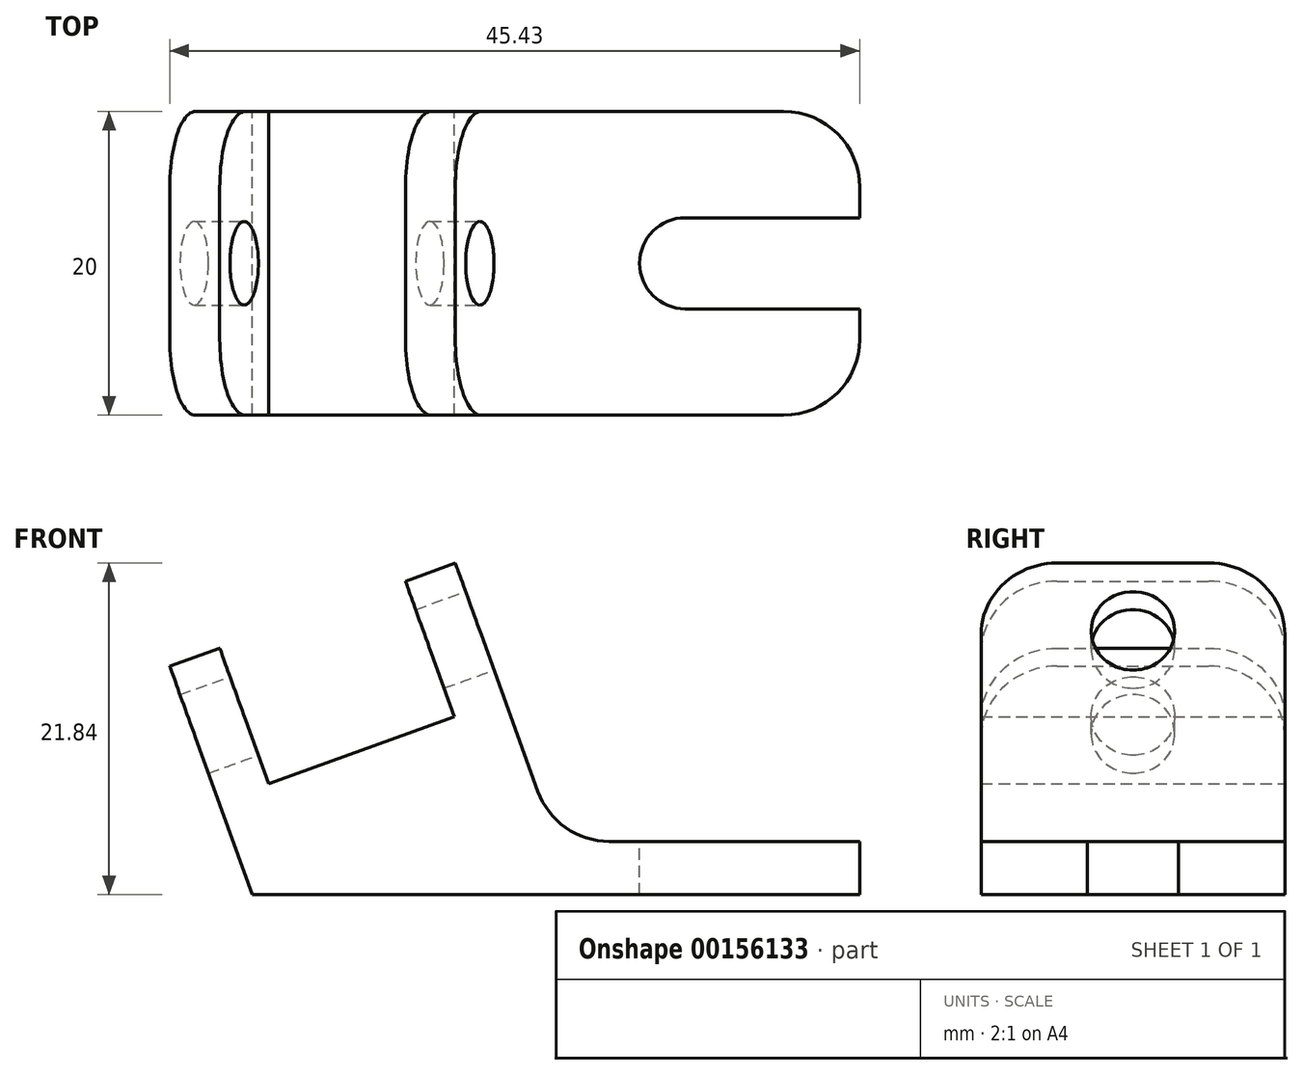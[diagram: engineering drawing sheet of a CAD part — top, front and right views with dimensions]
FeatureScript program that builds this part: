
annotation { "Feature Type Name" : "Feature", "Feature Type Description" : "" }
export const myFeature = defineFeature(function(context is Context, id is Id, definition is map)
    precondition{}
    {
        {
            var Q0;
            Q0=qCreatedBy(makeId("Front.planeOp"),FACE);
            var sketch = newSketch(context, id + "F0", { "sketchPlane" : qUnion([Q0])});
            skLineSegment(sketch, "E0", {"start": v(0, 0) * mm, "end": v(40, 0) * mm});
            skLineSegment(sketch, "E1", {"start": v(40, 0) * mm, "end": v(40, 3.5) * mm});
            skLineSegment(sketch, "E2", {"start": v(40, 3.5) * mm, "end": v(23.51, 3.5) * mm});
            skLineSegment(sketch, "E3", {"start": v(18.8, 6.8) * mm, "end": v(13.38, 21.84) * mm});
            skLineSegment(sketch, "E4", {"start": v(13.38, 21.84) * mm, "end": v(10.09, 20.65) * mm});
            skLineSegment(sketch, "E5", {"start": v(10.09, 20.65) * mm, "end": v(13.31, 11.72) * mm});
            skLineSegment(sketch, "E6", {"start": v(13.31, 11.72) * mm, "end": v(1.08, 7.3) * mm});
            skLineSegment(sketch, "E7", {"start": v(1.08, 7.3) * mm, "end": v(-2.14, 16.24) * mm});
            skLineSegment(sketch, "E8", {"start": v(-2.14, 16.24) * mm, "end": v(-5.43, 15.05) * mm});
            skLineSegment(sketch, "E9", {"start": v(-5.43, 15.05) * mm, "end": v(0, 0) * mm});
            skPoint(sketch, "E10.visualSharp", {"position": v(20, 3.5) * mm});
            skArc(sketch, "E10.filletArc", {"start": v(18.8, 6.8) * mm, "mid": v(20.64, 4.4) * mm, "end": v(23.51, 3.5) * mm});
            skSolve(sketch);
        }
        {
            var Q0;
            Q0=makeQuery(id+"F0.imprint","IMPRINT",FACE,{"disambiguationData":[TD([[makeQuery(id+"F0.imprint","IMPRINT",EDGE,{"derivedFrom":sQuery(id+"F0.wireOp",EDGE,"E0")}),1.0]])]});
            extrude(context, id + "F1", {"entities" : qUnion([Q0]), "endBound" : BoundingType.SYMMETRIC, "depth" : 20 * mm});
        }
        {
            var Q0;
            Q0=makeQuery(id+"F1.opExtrude","CAP_EDGE",EDGE,{"disambiguationData":[OSD([sQuery(id+"F0.wireOp",EDGE,"E8")])],"isStart":true});
            var Q1;
            Q1=makeQuery(id+"F1.opExtrude","CAP_EDGE",EDGE,{"disambiguationData":[OSD([sQuery(id+"F0.wireOp",EDGE,"E4")])],"isStart":true});
            var Q2;
            Q2=makeQuery(id+"F1.opExtrude","CAP_EDGE",EDGE,{"disambiguationData":[OSD([sQuery(id+"F0.wireOp",EDGE,"E4")])],"isStart":false});
            var Q3;
            Q3=makeQuery(id+"F1.opExtrude","CAP_EDGE",EDGE,{"disambiguationData":[OSD([sQuery(id+"F0.wireOp",EDGE,"E8")])],"isStart":false});
            var Q4;
            Q4=makeQuery(id+"F1.opExtrude","CAP_EDGE",EDGE,{"disambiguationData":[OSD([sQuery(id+"F0.wireOp",EDGE,"E1")])],"isStart":false});
            var Q5;
            Q5=makeQuery(id+"F1.opExtrude","CAP_EDGE",EDGE,{"disambiguationData":[OSD([sQuery(id+"F0.wireOp",EDGE,"E1")])],"isStart":true});
            fillet(context, id + "F2", {"entities" : qUnion([Q0, Q1, Q2, Q3, Q4, Q5]), "radius" : 5 * mm, "tangentPropagation" : true, "allowEdgeOverflow" : false});
        }
        {
            var Q0;
            Q0=makeQuery(id+"F1.opExtrude","SWEPT_FACE",FACE,{"disambiguationData":[OSD([sQuery(id+"F0.wireOp",EDGE,"E3")])]});
            var sketch = newSketch(context, id + "F3", { "sketchPlane" : qUnion([Q0])});
            skCircle(sketch, "E11", {"center": v(0, 11.25) * mm, "radius": 2.75 * mm});
            skPoint(sketch, "E11.centerSnap0", {"position": v(0, 16) * mm});
            skSolve(sketch);
        }
        {
            var Q0;
            Q0 = qSketchRegion(id + "F3", true);
            var Q1;
            Q1=makeQuery(id+"F1.opExtrude","SWEPT_FACE",FACE,{"disambiguationData":[OSD([sQuery(id+"F0.wireOp",EDGE,"E9")])]});
            extrude(context, id + "F4", {"entities" : qUnion([Q0]), "operationType" : NewBodyOperationType.REMOVE, "endBound" : BoundingType.UP_TO_SURFACE, "oppositeDirection" : true, "endBoundEntityFace" : qUnion([Q1]), "depth" : 25 * mm});
        }
        {
            var Q0;
            Q0=makeQuery(id+"F1.opExtrude","SWEPT_FACE",FACE,{"disambiguationData":[OSD([sQuery(id+"F0.wireOp",EDGE,"E2")])]});
            var sketch = newSketch(context, id + "F5", { "sketchPlane" : qUnion([Q0])});
            skCircle(sketch, "E12", {"center": v(28.51, 0) * mm, "radius": 3 * mm});
            skPoint(sketch, "E12.centerSnap0", {"position": v(40, 0) * mm});
            skLineSegment(sketch, "E13", {"start": v(28.51, 3) * mm, "end": v(40, 3) * mm});
            skLineSegment(sketch, "E14", {"start": v(28.51, -3) * mm, "end": v(40, -3) * mm});
            skSolve(sketch);
        }
        {
            var Q0;
            Q0 = qSketchRegion(id + "F5", true);
            var Q1;
            {var subQ0=sQuery(id+"F5.wireOp",EDGE,"E13");Q1=makeQuery(id+"F5.imprint","IMPRINT",FACE,{"disambiguationData":[TD([[makeQuery(id+"F5.imprint","IMPRINT",EDGE,{"derivedFrom":subQ0}),-1.0]])]});}
            var Q2;
            Q2=makeQuery(id+"F1.opExtrude","SWEPT_FACE",FACE,{"disambiguationData":[OSD([sQuery(id+"F0.wireOp",EDGE,"E0")])]});
            extrude(context, id + "F6", {"entities" : qUnion([Q0, Q1]), "operationType" : NewBodyOperationType.REMOVE, "endBound" : BoundingType.UP_TO_SURFACE, "oppositeDirection" : true, "endBoundEntityFace" : qUnion([Q2]), "depth" : 25 * mm});
        }
    });
